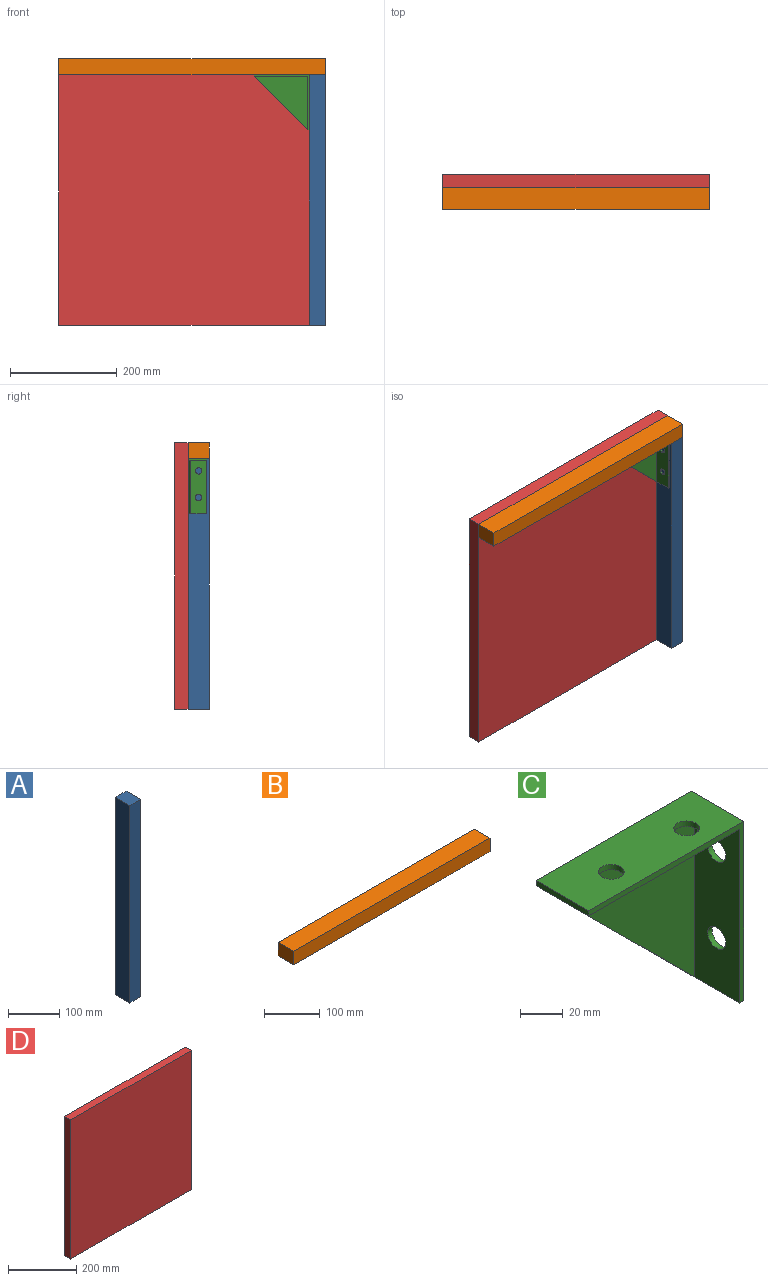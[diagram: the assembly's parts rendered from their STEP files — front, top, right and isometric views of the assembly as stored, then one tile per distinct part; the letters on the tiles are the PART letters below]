
ASSEMBLY  parts=4 mates=3
PART A: 6 faces, bbox 30x40x470 mm
  f0: plane 470x40mm, normal (1,0,0), area 18800mm2, adj f1,f3,f4,f5
  f1: plane 40x30mm, normal (0,0,1), area 1200mm2, adj f0,f2,f4,f5
  f2: plane 470x40mm, normal (-1,0,0), area 18800mm2, adj f1,f3,f4,f5
  f3: plane 40x30mm, normal (0,0,-1), area 1200mm2, adj f0,f2,f4,f5
  f4: plane 470x30mm, normal (0,-1,0), area 14100mm2, adj f0,f1,f2,f3
  f5: plane 470x30mm, normal (0,1,0), area 14100mm2, adj f0,f1,f2,f3
PART B: 6 faces, bbox 500x40x30 mm
  f0: plane 40x30mm, normal (-1,0,0), area 1200mm2, adj f1,f3,f4,f5
  f1: plane 500x40mm, normal (0,0,-1), area 20000mm2, adj f0,f2,f4,f5
  f2: plane 40x30mm, normal (1,0,0), area 1200mm2, adj f1,f3,f4,f5
  f3: plane 500x40mm, normal (0,0,1), area 20000mm2, adj f0,f2,f4,f5
  f4: plane 500x30mm, normal (0,-1,0), area 15000mm2, adj f0,f1,f2,f3
  f5: plane 500x30mm, normal (0,1,0), area 15000mm2, adj f0,f1,f2,f3
PART C: 14 faces, bbox 103x35x103 mm
  f0: plane 103x35mm, normal (0,0,1), area 3378.8mm2, adj f1,f3,f6,f9,f10,f11
  f1: plane 35x3mm, normal (-1,0,0), area 105mm2, adj f0,f4,f6,f7,f9
  f2: plane 35x3mm, normal (0,0,-1), area 105mm2, adj f3,f4,f6,f8,f9
  f3: plane 103x35mm, normal (1,0,0), area 3378.8mm2, adj f0,f2,f6,f9,f12,f13
  f4: plane 100x100mm, normal (-0.71,0,-0.71), area 707.1mm2, adj f1,f2,f5,f6
  f5: plane 100x100mm, normal (0,-1,0), area 5000mm2, adj f4,f7,f8
  f6: plane 103x103mm, normal (0,1,0), area 5609mm2, adj f0,f1,f2,f3,f4
  f7: plane 100x30mm, normal (0,0,-1), area 2773.8mm2, adj f1,f5,f8,f9,f10,f11
  f8: plane 100x30mm, normal (-1,0,0), area 2773.8mm2, adj f2,f5,f7,f9,f12,f13
  f9: plane 103x103mm, normal (0,-1,0), area 609mm2, adj f0,f1,f2,f3,f7,f8
  f10: cylinder r=6mm len=12mm, axis (0,0,-1), area 113.1mm2, adj f0,f7
  f11: cylinder r=6mm len=12mm, axis (0,0,-1), area 113.1mm2, adj f0,f7
  f12: cylinder r=6mm len=12mm, axis (-1,0,0), area 113.1mm2, adj f3,f8
  f13: cylinder r=6mm len=12mm, axis (-1,0,0), area 113.1mm2, adj f3,f8
PART D: 6 faces, bbox 500x25x500 mm
  f0: plane 500x25mm, normal (-1,0,0), area 12500mm2, adj f1,f3,f4,f5
  f1: plane 500x25mm, normal (0,0,-1), area 12500mm2, adj f0,f2,f4,f5
  f2: plane 500x25mm, normal (1,0,0), area 12500mm2, adj f1,f3,f4,f5
  f3: plane 500x25mm, normal (0,0,1), area 12500mm2, adj f0,f2,f4,f5
  f4: plane 500x500mm, normal (0,1,0), area 250000mm2, adj f0,f1,f2,f3
  f5: plane 500x500mm, normal (0,-1,0), area 250000mm2, adj f0,f1,f2,f3
PLACE A at identity fixed
PLACE B at identity fixed
PLACE C t=(467,0,467)mm
PLACE D at identity fixed
MATE planar A.f2 <-> C.f3  axis (-1,0,0) through (470,-20,235)mm
MATE planar B.f1 <-> C.f0  axis (0,0,-1) through (250,-20,470)mm
MATE planar C.f6 <-> D.f5  axis (0,1,0) through (434.69,0,434.69)mm
